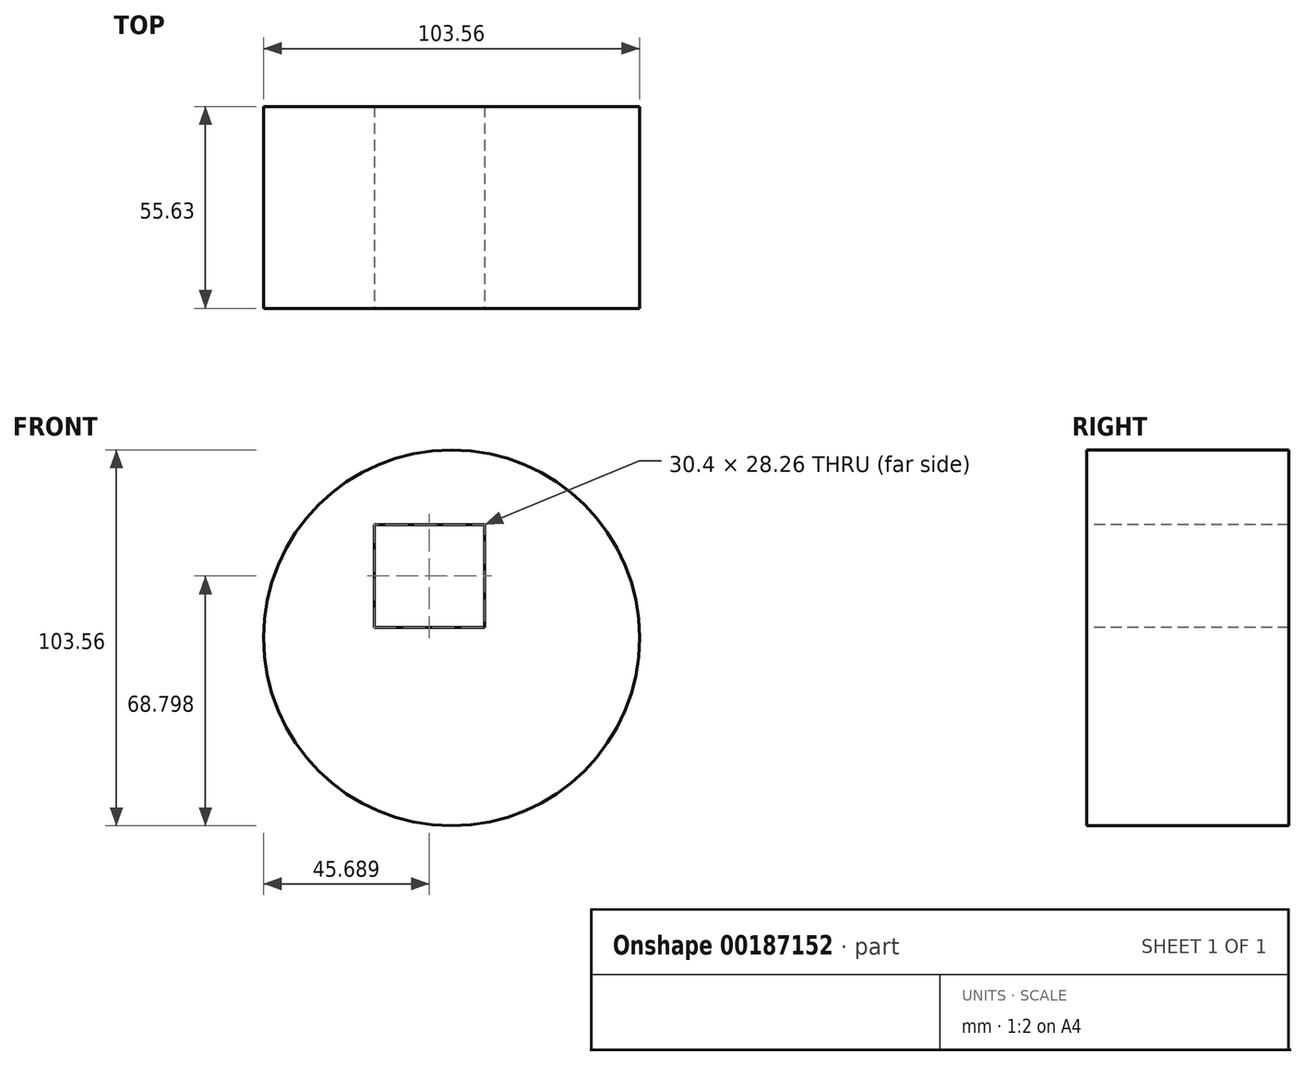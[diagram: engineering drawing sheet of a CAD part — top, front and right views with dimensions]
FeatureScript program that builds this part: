
annotation { "Feature Type Name" : "Feature", "Feature Type Description" : "" }
export const myFeature = defineFeature(function(context is Context, id is Id, definition is map)
    precondition{}
    {
        {
            var Q0;
            Q0=qCreatedBy(makeId("Front.planeOp"),FACE);
            var sketch = newSketch(context, id + "F0", { "sketchPlane" : qUnion([Q0])});
            skCircle(sketch, "E0", {"center": v(0, 0) * mm, "radius": 51.78 * mm});
            skSolve(sketch);
        }
        {
            var Q0;
            Q0=makeQuery(id+"F0.imprint","IMPRINT",FACE,{"disambiguationData":[TD([[makeQuery(id+"F0.imprint","IMPRINT",EDGE,{"derivedFrom":sQuery(id+"F0.wireOp",EDGE,"E0")}),1.0]])]});
            extrude(context, id + "F1", {"entities" : qUnion([Q0]), "depth" : 55.63 * mm});
        }
        {
            var Q0;
            Q0=makeQuery(id+"F1.opExtrude","CAP_FACE",FACE,{"disambiguationData":[OSD([sQuery(id+"F0.wireOp",EDGE,"E0")])],"isStart":false});
            var sketch = newSketch(context, id + "F2", { "sketchPlane" : qUnion([Q0])});
            skLineSegment(sketch, "E1.bottom", {"start": v(9.11, 2.89) * mm, "end": v(-21.3, 2.89) * mm});
            skLineSegment(sketch, "E1.top", {"start": v(9.11, 31.15) * mm, "end": v(-21.3, 31.15) * mm});
            skLineSegment(sketch, "E1.left", {"start": v(9.11, 2.89) * mm, "end": v(9.11, 31.15) * mm});
            skLineSegment(sketch, "E1.right", {"start": v(-21.3, 2.89) * mm, "end": v(-21.3, 31.15) * mm});
            skSolve(sketch);
        }
        {
            var Q0;
            Q0 = qSketchRegion(id + "F2", true);
            extrude(context, id + "F3", {"entities" : qUnion([Q0]), "operationType" : NewBodyOperationType.REMOVE, "oppositeDirection" : true, "depth" : 111 * mm});
        }
    });
